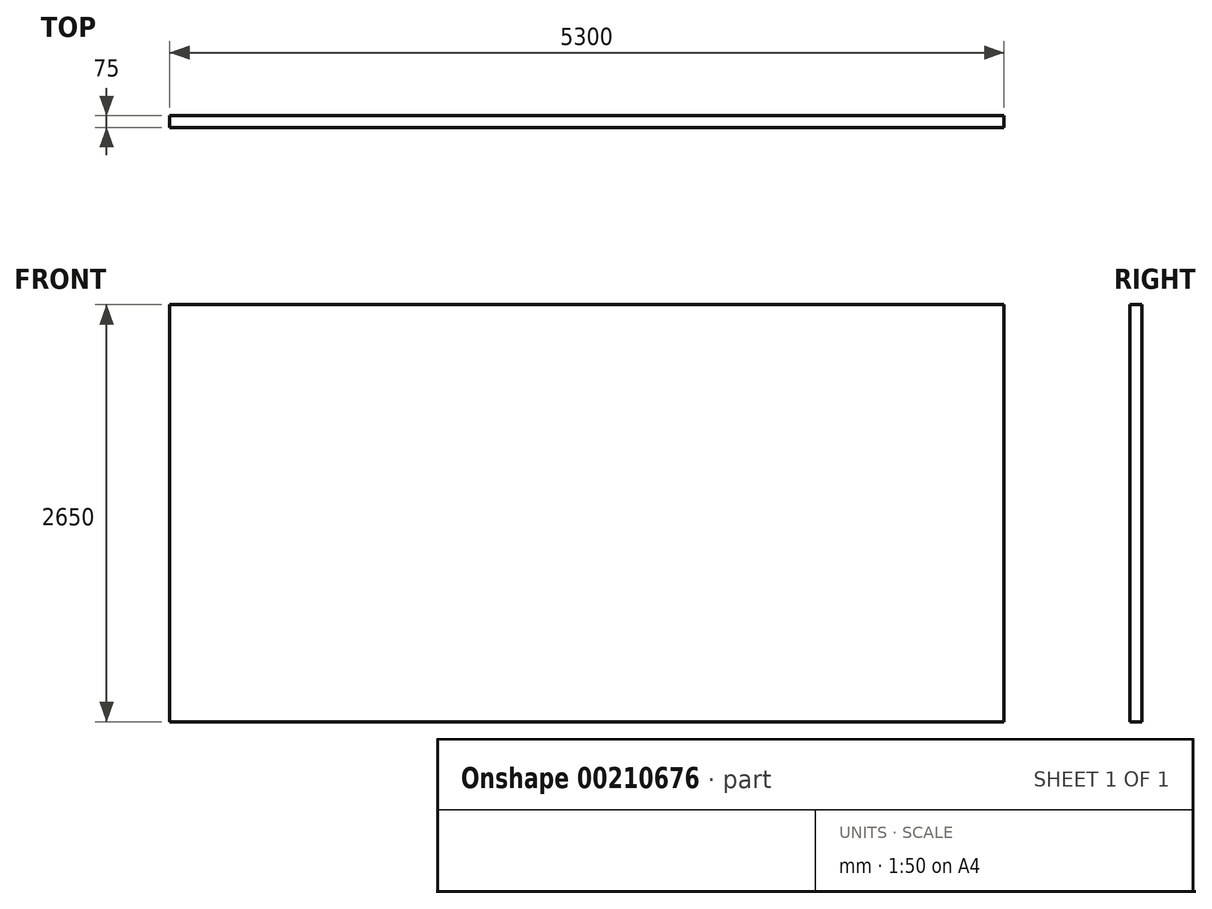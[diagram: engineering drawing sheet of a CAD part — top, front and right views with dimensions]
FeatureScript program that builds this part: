
annotation { "Feature Type Name" : "Feature", "Feature Type Description" : "" }
export const myFeature = defineFeature(function(context is Context, id is Id, definition is map)
    precondition{}
    {
        {
            var Q0;
            Q0=qCreatedBy(makeId("Front.planeOp"),FACE);
            var sketch = newSketch(context, id + "F0", { "sketchPlane" : qUnion([Q0])});
            skLineSegment(sketch, "E0.bottom", {"start": v(0, 0) * mm, "end": v(5300, 0) * mm});
            skLineSegment(sketch, "E0.top", {"start": v(0, 2650) * mm, "end": v(5300, 2650) * mm});
            skLineSegment(sketch, "E0.left", {"start": v(0, 0) * mm, "end": v(0, 2650) * mm});
            skLineSegment(sketch, "E0.right", {"start": v(5300, 0) * mm, "end": v(5300, 2650) * mm});
            skSolve(sketch);
        }
        {
            var Q0;
            Q0=makeQuery(id+"F0.imprint","IMPRINT",FACE,{"disambiguationData":[TD([[makeQuery(id+"F0.imprint","IMPRINT",EDGE,{"derivedFrom":sQuery(id+"F0.wireOp",EDGE,"E0.bottom")}),1.0]])]});
            extrude(context, id + "F1", {"entities" : qUnion([Q0]), "depth" : 75 * mm});
        }
    });
